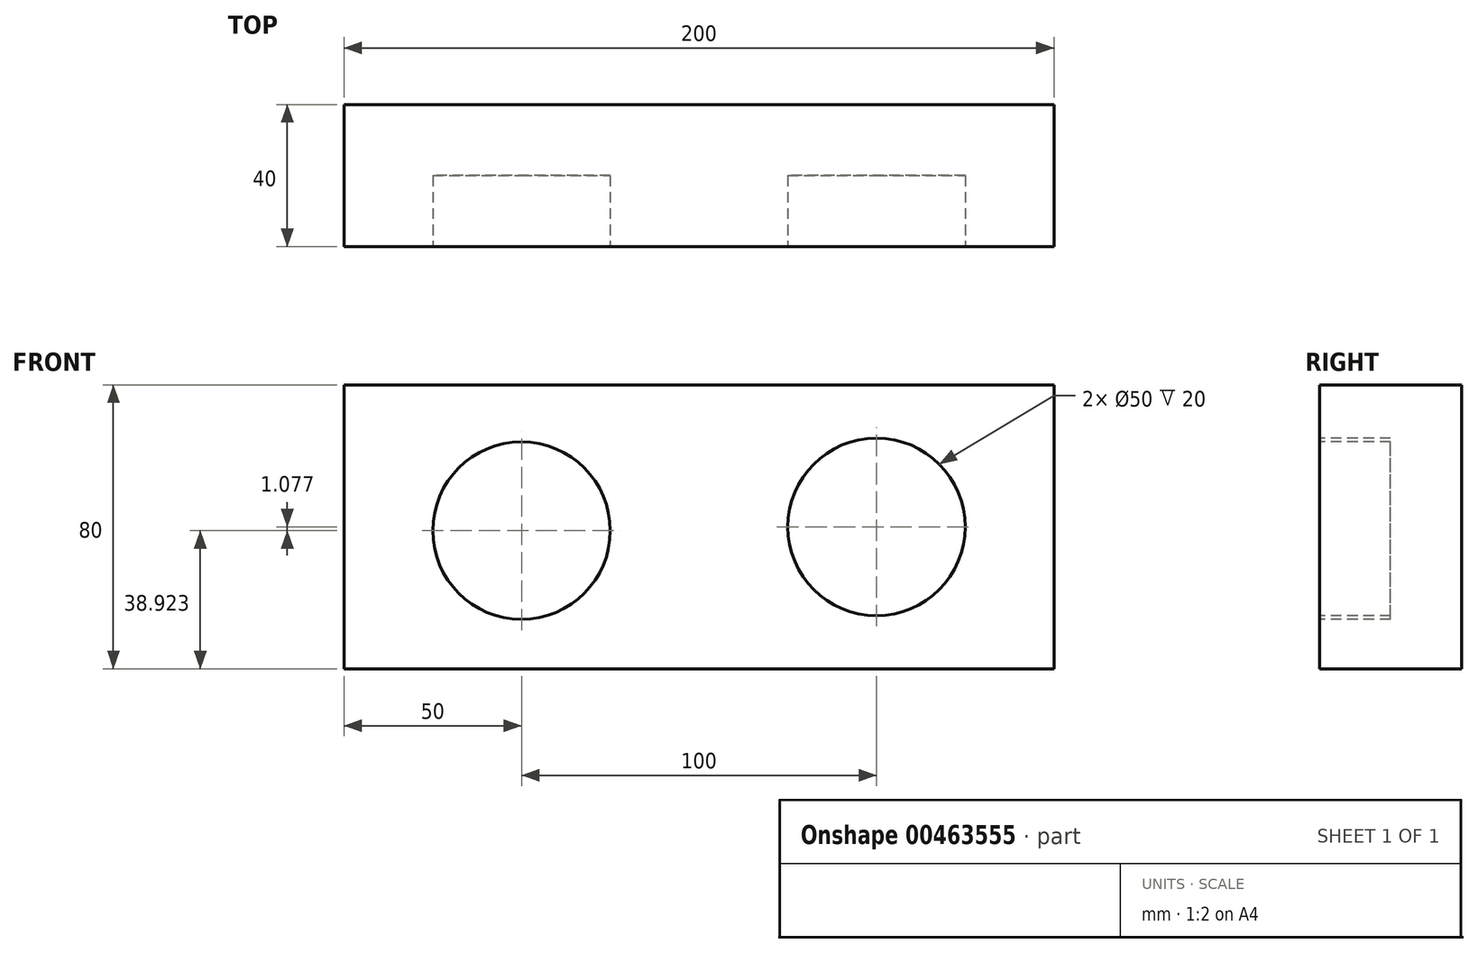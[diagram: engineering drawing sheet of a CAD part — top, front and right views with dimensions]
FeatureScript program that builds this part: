
annotation { "Feature Type Name" : "Feature", "Feature Type Description" : "" }
export const myFeature = defineFeature(function(context is Context, id is Id, definition is map)
    precondition{}
    {
        {
            var Q0;
            Q0=qCreatedBy(makeId("Front.planeOp"),FACE);
            var sketch = newSketch(context, id + "F0", { "sketchPlane" : qUnion([Q0])});
            skLineSegment(sketch, "E0.bottom", {"start": v(100, 40) * mm, "end": v(-100, 40) * mm});
            skLineSegment(sketch, "E0.top", {"start": v(100, -40) * mm, "end": v(-100, -40) * mm});
            skLineSegment(sketch, "E0.left", {"start": v(100, 40) * mm, "end": v(100, -40) * mm});
            skLineSegment(sketch, "E0.right", {"start": v(-100, 40) * mm, "end": v(-100, -40) * mm});
            skPoint(sketch, "E0.middle", {"position": v(0, 0) * mm});
            skSolve(sketch);
        }
        {
            var Q0;
            Q0=makeQuery(id+"F0.imprint","IMPRINT",FACE,{"disambiguationData":[TD([[makeQuery(id+"F0.imprint","IMPRINT",EDGE,{"derivedFrom":sQuery(id+"F0.wireOp",EDGE,"E0.bottom")}),1.0]])]});
            extrude(context, id + "F1", {"entities" : qUnion([Q0]), "depth" : 40 * mm, "offsetDistance" : 25 * mm});
        }
        {
            var Q0;
            Q0=makeQuery(id+"F1.opExtrude","CAP_FACE",FACE,{"disambiguationData":[OSD([sQuery(id+"F0.wireOp",EDGE,"E0.bottom"),sQuery(id+"F0.wireOp",EDGE,"E0.top"),sQuery(id+"F0.wireOp",EDGE,"E0.left"),sQuery(id+"F0.wireOp",EDGE,"E0.right")])],"isStart":false});
            var sketch = newSketch(context, id + "F2", { "sketchPlane" : qUnion([Q0])});
            skCircle(sketch, "E1", {"center": v(50, 0) * mm, "radius": 25 * mm});
            skCircle(sketch, "E2", {"center": v(-50, -1.08) * mm, "radius": 25 * mm});
            skSolve(sketch);
        }
        {
            var Q0;
            Q0 = qSketchRegion(id + "F2", true);
            var Q1;
            Q1=sQuery(id+"F2.wireOp",EDGE,"E2");
            var Q2;
            Q2=sQuery(id+"F2.wireOp",EDGE,"E1");
            extrude(context, id + "F3", {"entities" : qUnion([Q0]), "operationType" : NewBodyOperationType.REMOVE, "surfaceEntities" : qUnion([Q1, Q2]), "oppositeDirection" : true, "depth" : 40 * mm, "offsetDistance" : 25 * mm, "symmetric" : true});
        }
    });
